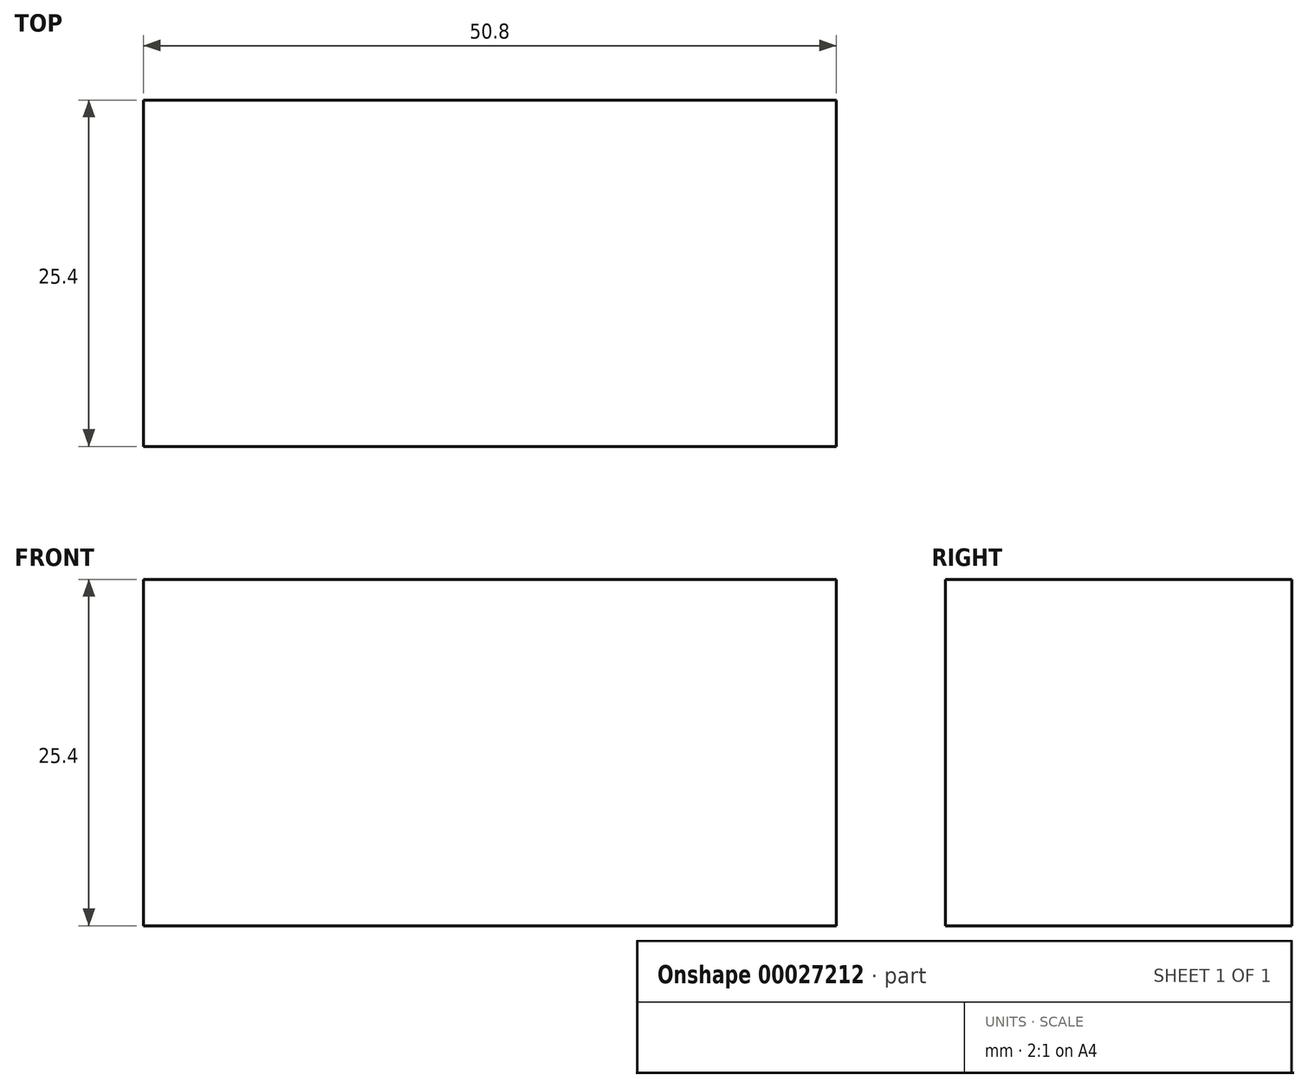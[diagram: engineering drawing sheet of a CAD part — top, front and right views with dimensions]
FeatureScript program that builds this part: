
annotation { "Feature Type Name" : "Feature", "Feature Type Description" : "" }
export const myFeature = defineFeature(function(context is Context, id is Id, definition is map)
    precondition{}
    {
        {
            var Q0;
            Q0=qCreatedBy(makeId("Front.planeOp"),FACE);
            var sketch = newSketch(context, id + "F0", { "sketchPlane" : qUnion([Q0])});
            skLineSegment(sketch, "E0.bottom", {"start": v(0, 0) * mm, "end": v(50.8, 0) * mm});
            skLineSegment(sketch, "E0.top", {"start": v(0, 25.4) * mm, "end": v(50.8, 25.4) * mm});
            skLineSegment(sketch, "E0.left", {"start": v(0, 0) * mm, "end": v(0, 25.4) * mm});
            skLineSegment(sketch, "E0.right", {"start": v(50.8, 0) * mm, "end": v(50.8, 25.4) * mm});
            skSolve(sketch);
        }
        {
            var Q0;
            Q0=makeQuery(id+"F0.imprint","IMPRINT",FACE,{"disambiguationData":[TD([[makeQuery(id+"F0.imprint","IMPRINT",EDGE,{"derivedFrom":sQuery(id+"F0.wireOp",EDGE,"E0.bottom")}),1.0]])]});
            extrude(context, id + "F1", {"entities" : qUnion([Q0]), "depth" : 25.4 * mm});
        }
    });
